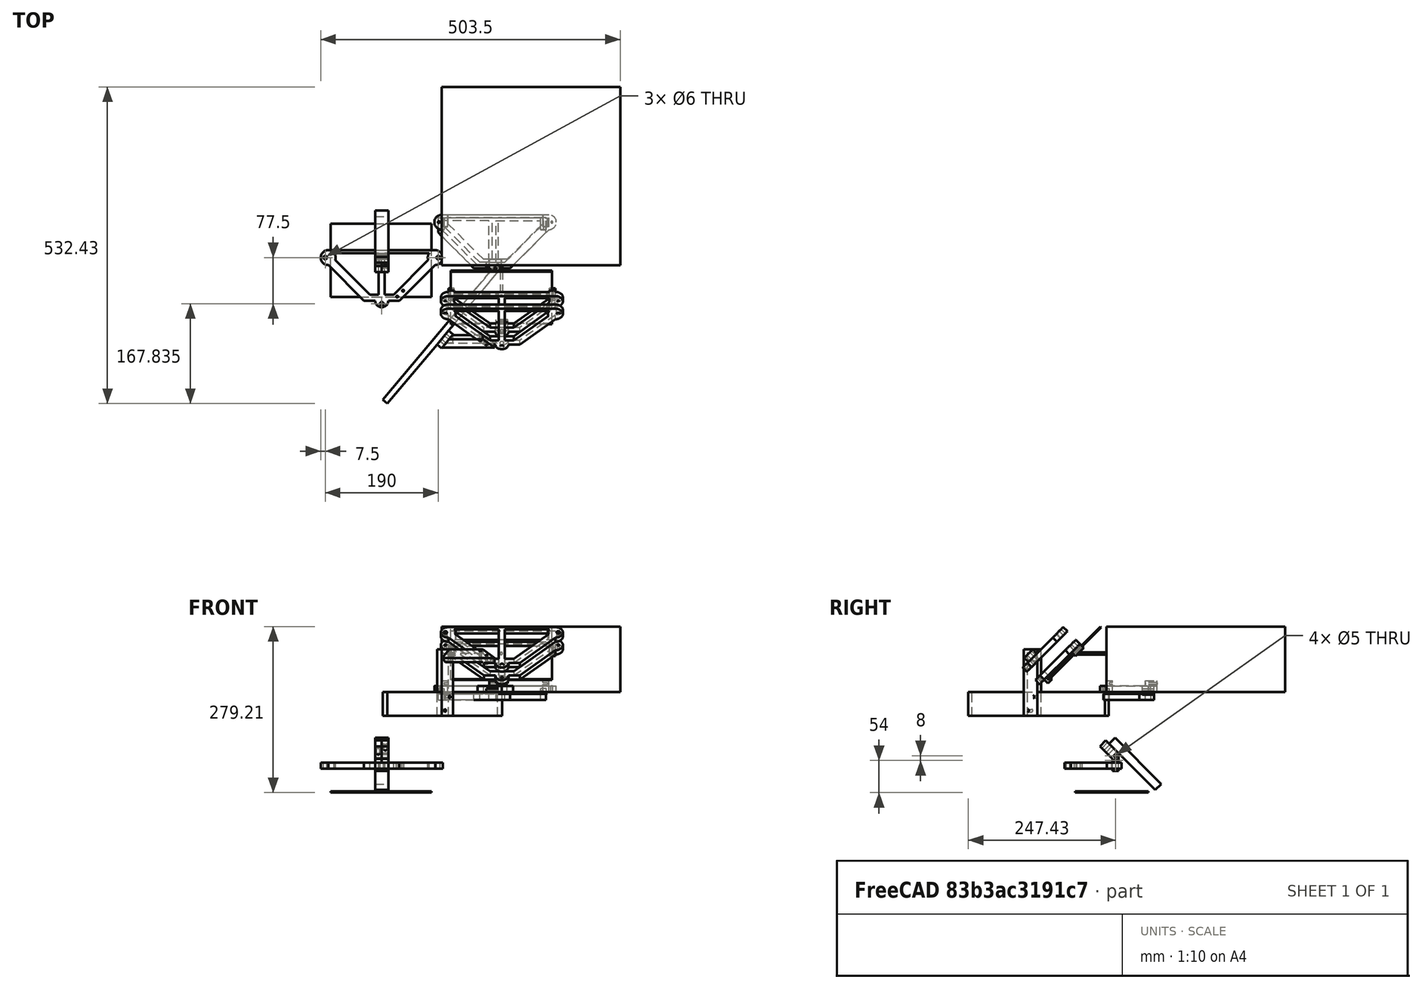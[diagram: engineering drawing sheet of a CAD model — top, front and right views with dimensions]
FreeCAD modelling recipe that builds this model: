
FCSTD DOCUMENT  (FreeCAD 0.19R24276 (Git))
Label: mirror-mount
License: All rights reserved
LicenseURL: http://en.wikipedia.org/wiki/All_rights_reserved
objects: Part::Box×51, Part::Cylinder×41, Part::MultiFuse×32, Part::Cut×29, Part::Chamfer×13, Part::Mirroring×2, App::DocumentObjectGroup×1, Part::MultiCommon×1
note: 169 computed .brp shape members not serialized (recipe doc carries the construction recipe); baked Part::Feature solids carry a one-line shape summary decoded from their .brp

FEATURE [Part::Box] Box  label="Mirror"
  AttacherType = Attacher::AttachEngine3D
  Height = 2
  Length = 170
  Placement = pos=(185,-99,22) rot=(0,0.924261,0.38176;3.14159rad)
  Width = 125
FEATURE [Part::Box] Box001  label="Cube001"
  AttacherType = Attacher::AttachEngine3D
  Height = 10
  Length = 10
  Placement = pos=(-5,0,-4) rot=(0,0,1;0rad)
  Width = 20
FEATURE [Part::Box] Box002  label="Cube002"
  AttacherType = Attacher::AttachEngine3D
  Height = 3
  Length = 10
  Placement = pos=(0,-3,-1) rot=(0,0,1;0rad)
  Width = 26
FEATURE [Part::Cut] Cut
  Base = -> Box001
  Placement = pos=(-1,60,0) rot=(0,0,1;0rad)
  Tool = -> Box002
FEATURE [Part::Box] Box003  label="Cube003"
  AttacherType = Attacher::AttachEngine3D
  Height = 10
  Length = 10
  Placement = pos=(-5,0,-4) rot=(0,0,1;0rad)
  Width = 20
FEATURE [Part::Box] Box004  label="Cube004"
  AttacherType = Attacher::AttachEngine3D
  Height = 3
  Length = 10
  Placement = pos=(0,-3,-1) rot=(0,0,1;0rad)
  Width = 26
FEATURE [Part::Cut] Cut001
  Base = -> Box003
  Placement = pos=(0,60,0) rot=(0,0,1;0rad)
  Tool = -> Box004
FEATURE [Part::Box] Box005  label="Cube005"
  AttacherType = Attacher::AttachEngine3D
  Height = 10
  Length = 10
  Placement = pos=(-5,0,-4) rot=(0,0,1;0rad)
  Width = 20
FEATURE [Part::Box] Box006  label="Cube006"
  AttacherType = Attacher::AttachEngine3D
  Height = 3
  Length = 10
  Placement = pos=(0,-3,-1) rot=(0,0,1;0rad)
  Width = 26
FEATURE [Part::Cut] Cut002
  Base = -> Box005
  Placement = pos=(95,0,0) rot=(0,0,1;1.5708rad)
  Tool = -> Box006
FEATURE [Part::Mirroring] Part__Mirroring  label="Cut001 (Mirror #1)"
  Base = (0,0,0)
  Normal = (1,0,0)
  Placement = pos=(171,0,0) rot=(0,0,1;0rad)
  Source = -> Cut001
FEATURE [Part::Box] Box007  label="Cube007"
  AttacherType = Attacher::AttachEngine3D
  Height = 10
  Length = 181
  Placement = pos=(-6,-5,-13) rot=(0,0,1;0rad)
  Width = 85
FEATURE [Part::Chamfer] Chamfer
  Base = -> Box007
  Edges = 1 edges r=60: [Edge1]
FEATURE [Part::Chamfer] Chamfer001
  Base = -> Chamfer
  Edges = 1 edges r=60: [Edge15]
FEATURE [Part::Box] Box008  label="Cube008"
  AttacherType = Attacher::AttachEngine3D
  Height = 25
  Length = 75
  Placement = pos=(4,5,-19) rot=(0,0,1;0rad)
  Width = 70
FEATURE [Part::Chamfer] Chamfer002
  Base = -> Box008
  Edges = 1 edges r=60: [Edge1]
FEATURE [Part::Box] Box009  label="Cube009"
  AttacherType = Attacher::AttachEngine3D
  Height = 25
  Length = 75
  Placement = pos=(4,5,-19) rot=(0,0,1;0rad)
  Width = 70
FEATURE [Part::Chamfer] Chamfer003
  Base = -> Box009
  Edges = 1 edges r=60: [Edge1]
FEATURE [Part::Mirroring] Part__Mirroring001  label="Chamfer003 (Mirror #2)"
  Base = (0,0,0)
  Normal = (1,0,0)
  Placement = pos=(170,0,0) rot=(0,0,1;0rad)
  Source = -> Chamfer003
FEATURE [Part::MultiFuse] Fusion
  Shapes = -> [Chamfer002,Part__Mirroring001]
FEATURE [Part::MultiFuse] Fusion001
  Shapes = -> [Chamfer001,Cut,Cut002,Part__Mirroring]
FEATURE [Part::Cut] Cut003
  Base = -> Fusion001
  Tool = -> Fusion
FEATURE [Part::Box] Box010  label="Projector"
  AttacherType = Attacher::AttachEngine3D
  Height = 110
  Length = 300
  Width = 300
FEATURE [Part::Cylinder] Cylinder  label="Lens Centre"
  Angle = 360
  AttacherType = Attacher::AttachEngine3D
  Height = 50
  Placement = pos=(100,0,65) rot=(1,0,0;1.5708rad)
  Radius = 2
FEATURE [Part::Box] Box011  label="Wooden Support"
  AttacherType = Attacher::AttachEngine3D
  Height = 40
  Length = 10
  Placement = pos=(-99,-226,-40) rot=(0,0,-1;0.698132rad)
  Width = 300
FEATURE [Part::Box] Box012  label="Cube012"
  AttacherType = Attacher::AttachEngine3D
  Height = 10
  Length = 180
  Width = 85
FEATURE [Part::Box] Box013  label="Cube013"
  AttacherType = Attacher::AttachEngine3D
  Height = 10
  Length = 10
  Placement = pos=(0,65,9) rot=(0,0,1;0rad)
  Width = 20
FEATURE [Part::Box] Box014  label="Cube014"
  AttacherType = Attacher::AttachEngine3D
  Height = 10
  Length = 20
  Placement = pos=(80,0,9) rot=(0,0,1;0rad)
  Width = 10
FEATURE [Part::Box] Box015  label="Cube015"
  AttacherType = Attacher::AttachEngine3D
  Height = 10
  Length = 10
  Placement = pos=(170,65,9) rot=(0,0,1;0rad)
  Width = 20
FEATURE [Part::Box] Box016  label="Cube016"
  AttacherType = Attacher::AttachEngine3D
  Height = 3
  Length = 26
  Placement = pos=(76.5,5,13) rot=(0,0,1;0rad)
  Width = 10
FEATURE [Part::Cut] Cut004
  Base = -> Box014
  Tool = -> Box016
FEATURE [Part::Box] Box017  label="Cube017"
  AttacherType = Attacher::AttachEngine3D
  Height = 3
  Length = 10
  Placement = pos=(167.5,62,13) rot=(0,0,1;0rad)
  Width = 26
FEATURE [Part::Box] Box018  label="Cube018"
  AttacherType = Attacher::AttachEngine3D
  Height = 3
  Length = 10
  Placement = pos=(3.5,62,13) rot=(0,0,1;0rad)
  Width = 26
FEATURE [Part::Cut] Cut005
  Base = -> Box013
  Tool = -> Box018
FEATURE [Part::Cut] Cut006
  Base = -> Box015
  Tool = -> Box017
FEATURE [Part::Chamfer] Chamfer004
  Base = -> Box012
  Edges = 2 edges r=60: [Edge1,Edge5]
FEATURE [Part::Box] Box019  label="Cube019"
  AttacherType = Attacher::AttachEngine3D
  Height = 25
  Length = 75
  Placement = pos=(10,10,-6) rot=(0,0,1;0rad)
  Width = 70
FEATURE [Part::Box] Box020  label="Cube020"
  AttacherType = Attacher::AttachEngine3D
  Height = 25
  Length = 75
  Placement = pos=(95,10,-6) rot=(0,0,1;0rad)
  Width = 70
FEATURE [Part::MultiFuse] Fusion002  label="Square Holes"
  Shapes = -> [Box019,Box020]
FEATURE [Part::Chamfer] Chamfer005  label="Chamfer Square Holes"
  Base = -> Fusion002
  Edges = 2 edges r=60: [Edge1,Edge17]
FEATURE [Part::MultiFuse] Fusion003  label="Square Clips"
  Shapes = -> [Cut006,Cut005,Cut004]
FEATURE [App::DocumentObjectGroup] Group  label="Old"
  Group = -> [Cut003]
FEATURE [Part::Box] Box021  label="Cube021"
  AttacherType = Attacher::AttachEngine3D
  Height = 10
  Length = 180
  Placement = pos=(0,0,-30) rot=(0,0,1;0rad)
  Width = 85
FEATURE [Part::Box] Box022  label="Cube022"
  AttacherType = Attacher::AttachEngine3D
  Height = 25
  Length = 75
  Placement = pos=(10,10,-37) rot=(0,0,1;0rad)
  Width = 70
FEATURE [Part::Chamfer] Chamfer006
  Base = -> Box021
  Edges = 2 edges r=60: [Edge1,Edge5]
FEATURE [Part::Box] Box023  label="Cube023"
  AttacherType = Attacher::AttachEngine3D
  Height = 25
  Length = 75
  Placement = pos=(95,10,-37) rot=(0,0,1;0rad)
  Width = 70
FEATURE [Part::MultiFuse] Fusion005
  Shapes = -> [Box022,Box023]
FEATURE [Part::Chamfer] Chamfer007
  Base = -> Fusion005
  Edges = 2 edges r=60: [Edge1,Edge17]
FEATURE [Part::Cut] Cut008
  Base = -> Chamfer006
  Tool = -> Chamfer007
FEATURE [Part::Cylinder] Cylinder001  label="Cylinder"
  Angle = 360
  AttacherType = Attacher::AttachEngine3D
  Height = 17
  Placement = pos=(90,-5,-6) rot=(0,0,1;0rad)
  Radius = 1.6
FEATURE [Part::Cylinder] Cylinder002
  Angle = 360
  AttacherType = Attacher::AttachEngine3D
  Height = 10
  Placement = pos=(90,0,0) rot=(0,0,1;0rad)
  Radius = 11
FEATURE [Part::Cylinder] Cylinder003
  Angle = 360
  AttacherType = Attacher::AttachEngine3D
  Height = 10
  Placement = pos=(180,72.5,0) rot=(0,0,1;0rad)
  Radius = 12.5
FEATURE [Part::Cylinder] Cylinder004
  Angle = 360
  AttacherType = Attacher::AttachEngine3D
  Height = 10
  Placement = pos=(0,72.5,0) rot=(0,0,1;0rad)
  Radius = 12.5
FEATURE [Part::MultiFuse] Fusion006  label="Bumps"
  Shapes = -> [Cylinder002,Cylinder003,Cylinder004]
FEATURE [Part::MultiFuse] Fusion007
  Shapes = -> [Fusion006,Chamfer004]
FEATURE [Part::Cut] Cut009
  Base = -> Fusion007
  Tool = -> Chamfer005
FEATURE [Part::Cylinder] Cylinder005
  Angle = 360
  AttacherType = Attacher::AttachEngine3D
  Height = 17
  Placement = pos=(185,72.5,-2) rot=(0,0,1;0rad)
  Radius = 1.6
FEATURE [Part::Cylinder] Cylinder006
  Angle = 360
  AttacherType = Attacher::AttachEngine3D
  Height = 17
  Placement = pos=(-5,72.5,-3) rot=(0,0,1;0rad)
  Radius = 1.6
FEATURE [Part::MultiFuse] Fusion008  label="M3 ST Holes"
  Shapes = -> [Cylinder005,Cylinder001,Cylinder006]
FEATURE [Part::Cut] Cut010
  Base = -> Cut009
  Tool = -> Fusion008
FEATURE [Part::MultiFuse] Fusion009  label="Mount - laying flat"
  Shapes = -> [Cut010,Fusion003]
FEATURE [Part::Cylinder] Cylinder007
  Angle = 360
  AttacherType = Attacher::AttachEngine3D
  Height = 10
  Placement = pos=(90,0,-30) rot=(0,0,1;0rad)
  Radius = 11
FEATURE [Part::Cylinder] Cylinder008
  Angle = 360
  AttacherType = Attacher::AttachEngine3D
  Height = 10
  Placement = pos=(180,72.5,-30) rot=(0,0,1;0rad)
  Radius = 12.5
FEATURE [Part::Cylinder] Cylinder009
  Angle = 360
  AttacherType = Attacher::AttachEngine3D
  Height = 10
  Placement = pos=(0,72.5,-30) rot=(0,0,1;0rad)
  Radius = 12.5
FEATURE [Part::Cylinder] Cylinder010
  Angle = 360
  AttacherType = Attacher::AttachEngine3D
  Height = 17
  Placement = pos=(185,72.5,-33) rot=(0,0,1;0rad)
  Radius = 3
FEATURE [Part::Cylinder] Cylinder011
  Angle = 360
  AttacherType = Attacher::AttachEngine3D
  Height = 17
  Placement = pos=(90,-5,-33) rot=(0,0,1;0rad)
  Radius = 3
FEATURE [Part::Cylinder] Cylinder012
  Angle = 360
  AttacherType = Attacher::AttachEngine3D
  Height = 17
  Placement = pos=(-5,72.5,-33) rot=(0,0,1;0rad)
  Radius = 3
FEATURE [Part::MultiFuse] Fusion010  label="Bumps001"
  Shapes = -> [Cylinder007,Cylinder008,Cylinder009]
FEATURE [Part::MultiFuse] Fusion011  label="Large Holes"
  Shapes = -> [Cylinder010,Cylinder011,Cylinder012]
FEATURE [Part::MultiFuse] Fusion012
  Shapes = -> [Cut008,Fusion010]
FEATURE [Part::Cut] Cut011
  Base = -> Fusion012
  Placement = pos=(191,-112,28) rot=(0,0.924261,0.38176;3.14159rad)
  Tool = -> Fusion011
FEATURE [Part::Box] Box024  label="Cube024"
  AttacherType = Attacher::AttachEngine3D
  Height = 10
  Length = 180
  Width = 85
FEATURE [Part::Box] Box025  label="Cube025"
  AttacherType = Attacher::AttachEngine3D
  Height = 10
  Length = 10
  Placement = pos=(0,65,9) rot=(0,0,1;0rad)
  Width = 20
FEATURE [Part::Box] Box026  label="Cube026"
  AttacherType = Attacher::AttachEngine3D
  Height = 10
  Length = 20
  Placement = pos=(80,0,9) rot=(0,0,1;0rad)
  Width = 10
FEATURE [Part::Box] Box027  label="Cube027"
  AttacherType = Attacher::AttachEngine3D
  Height = 10
  Length = 10
  Placement = pos=(170,65,9) rot=(0,0,1;0rad)
  Width = 20
FEATURE [Part::Box] Box028  label="Cube028"
  AttacherType = Attacher::AttachEngine3D
  Height = 3
  Length = 26
  Placement = pos=(76.5,5,13) rot=(0,0,1;0rad)
  Width = 10
FEATURE [Part::Cut] Cut012
  Base = -> Box026
  Tool = -> Box028
FEATURE [Part::Box] Box029  label="Cube029"
  AttacherType = Attacher::AttachEngine3D
  Height = 3
  Length = 10
  Placement = pos=(167.5,62,13) rot=(0,0,1;0rad)
  Width = 26
FEATURE [Part::Box] Box030  label="Cube030"
  AttacherType = Attacher::AttachEngine3D
  Height = 3
  Length = 10
  Placement = pos=(3.5,62,13) rot=(0,0,1;0rad)
  Width = 26
FEATURE [Part::Cut] Cut013
  Base = -> Box025
  Tool = -> Box030
FEATURE [Part::Cut] Cut014
  Base = -> Box027
  Tool = -> Box029
FEATURE [Part::Chamfer] Chamfer008
  Base = -> Box024
  Edges = 2 edges r=60: [Edge1,Edge5]
FEATURE [Part::Box] Box031  label="Cube031"
  AttacherType = Attacher::AttachEngine3D
  Height = 25
  Length = 75
  Placement = pos=(10,10,-6) rot=(0,0,1;0rad)
  Width = 70
FEATURE [Part::Box] Box032  label="Cube032"
  AttacherType = Attacher::AttachEngine3D
  Height = 25
  Length = 75
  Placement = pos=(95,10,-6) rot=(0,0,1;0rad)
  Width = 70
FEATURE [Part::MultiFuse] Fusion013  label="Square Holes001"
  Shapes = -> [Box031,Box032]
FEATURE [Part::Chamfer] Chamfer009  label="Chamfer Square Holes001"
  Base = -> Fusion013
  Edges = 2 edges r=60: [Edge1,Edge17]
FEATURE [Part::MultiFuse] Fusion014  label="Square Clips001"
  Shapes = -> [Cut014,Cut013,Cut012]
FEATURE [Part::Cylinder] Cylinder013
  Angle = 360
  AttacherType = Attacher::AttachEngine3D
  Height = 17
  Placement = pos=(90,-5,-6) rot=(0,0,1;0rad)
  Radius = 1.6
FEATURE [Part::Cylinder] Cylinder014
  Angle = 360
  AttacherType = Attacher::AttachEngine3D
  Height = 10
  Placement = pos=(90,0,0) rot=(0,0,1;0rad)
  Radius = 11
FEATURE [Part::Cylinder] Cylinder015
  Angle = 360
  AttacherType = Attacher::AttachEngine3D
  Height = 10
  Placement = pos=(180,72.5,0) rot=(0,0,1;0rad)
  Radius = 12.5
FEATURE [Part::Cylinder] Cylinder016
  Angle = 360
  AttacherType = Attacher::AttachEngine3D
  Height = 10
  Placement = pos=(0,72.5,0) rot=(0,0,1;0rad)
  Radius = 12.5
FEATURE [Part::MultiFuse] Fusion015  label="Bumps002"
  Shapes = -> [Cylinder014,Cylinder015,Cylinder016]
FEATURE [Part::MultiFuse] Fusion016
  Shapes = -> [Fusion015,Chamfer008]
FEATURE [Part::Cut] Cut015
  Base = -> Fusion016
  Tool = -> Chamfer009
FEATURE [Part::Cylinder] Cylinder017
  Angle = 360
  AttacherType = Attacher::AttachEngine3D
  Height = 17
  Placement = pos=(185,72.5,-2) rot=(0,0,1;0rad)
  Radius = 1.6
FEATURE [Part::Cylinder] Cylinder018
  Angle = 360
  AttacherType = Attacher::AttachEngine3D
  Height = 17
  Placement = pos=(-5,72.5,-3) rot=(0,0,1;0rad)
  Radius = 1.6
FEATURE [Part::MultiFuse] Fusion017  label="M3 ST Holes001"
  Shapes = -> [Cylinder017,Cylinder013,Cylinder018]
FEATURE [Part::Cut] Cut016
  Base = -> Cut015
  Tool = -> Fusion017
FEATURE [Part::MultiFuse] Fusion018  label="Mount001"
  Placement = pos=(191,-112,28) rot=(0,0.924261,0.38176;3.14159rad)
  Shapes = -> [Cut016,Fusion014]
FEATURE [Part::Box] Box033  label="Wooden Support001"
  AttacherType = Attacher::AttachEngine3D
  Height = 112
  Length = 10
  Placement = pos=(-8,-133,-40) rot=(0,0,-1;0.698132rad)
  Width = 30
FEATURE [Part::Box] Box034  label="Cube"
  AttacherType = Attacher::AttachEngine3D
  Height = 10
  Length = 90
  Placement = pos=(89,-138.47,57.61) rot=(0,0.924261,0.38176;3.14159rad)
  Width = 20
FEATURE [Part::Box] Box035  label="Wooden Support002"
  AttacherType = Attacher::AttachEngine3D
  Height = 135
  Length = 10
  Placement = pos=(-20,-133,-40) rot=(0,0,-1;0.698132rad)
  Width = 30
FEATURE [Part::Cut] Cut017
  Base = -> Box034
  Tool = -> Box035
FEATURE [Part::Chamfer] Chamfer010
  Base = -> Cut017
  Edges = 1 edges r=19.99: [Edge3]
FEATURE [Part::Cylinder] Cylinder019
  Angle = 360
  AttacherType = Attacher::AttachEngine3D
  Height = 50
  Placement = pos=(75,-154,80) rot=(0,0.924261,0.38176;3.14159rad)
  Radius = 1.8
FEATURE [Part::Cylinder] Cylinder020
  Angle = 360
  AttacherType = Attacher::AttachEngine3D
  Height = 50
  Placement = pos=(65,-140,80) rot=(0,0.924261,0.38176;3.14159rad)
  Radius = 1.8
FEATURE [Part::Cylinder] Cylinder021
  Angle = 360
  AttacherType = Attacher::AttachEngine3D
  Height = 50
  Placement = pos=(75,-154,80) rot=(0,0.924261,0.38176;3.14159rad)
  Radius = 1.6
FEATURE [Part::Cylinder] Cylinder022
  Angle = 360
  AttacherType = Attacher::AttachEngine3D
  Height = 50
  Placement = pos=(65,-140,80) rot=(0,0.924261,0.38176;3.14159rad)
  Radius = 1.6
FEATURE [Part::MultiFuse] Fusion019  label="Clearance Holes"
  Shapes = -> [Cylinder019,Cylinder020]
FEATURE [Part::Cut] Cut018
  Base = -> Chamfer010
  Tool = -> Fusion019
FEATURE [Part::MultiFuse] Fusion020  label="M3 ST Holes002"
  Shapes = -> [Cylinder021,Cylinder022]
FEATURE [Part::Cut] Cut019  label="Mount Carrier"
  Base = -> Cut011
  Tool = -> Fusion020
FEATURE [Part::MultiFuse] Fusion021
  Shapes = -> [Cut018,Box033]
FEATURE [Part::Cylinder] Cylinder023
  Angle = 360
  AttacherType = Attacher::AttachEngine3D
  Height = 52
  Placement = pos=(25.77,-134.121,-8) rot=(0.68362,-0.255595,-0.68362;3.64207rad)
  Radius = 2.2
FEATURE [Part::Cylinder] Cylinder024
  Angle = 360
  AttacherType = Attacher::AttachEngine3D
  Height = 52
  Placement = pos=(7.77,-134.121,-31) rot=(0.68362,-0.255595,-0.68362;3.64207rad)
  Radius = 2.2
FEATURE [Part::MultiFuse] Fusion022  label="M4 Holes"
  Shapes = -> [Cylinder024,Cylinder023]
FEATURE [Part::Cut] Cut020
  Base = -> Fusion021
  Tool = -> Fusion022
FEATURE [Part::Box] Box036  label="Cube033"
  AttacherType = Attacher::AttachEngine3D
  Height = 13
  Length = 13
  Placement = pos=(5,-131,52) rot=(0,0,1;0rad)
  Width = 15
FEATURE [Part::Box] Box037  label="Wooden Support003"
  AttacherType = Attacher::AttachEngine3D
  Height = 135
  Length = 10
  Placement = pos=(-20,-133,-40) rot=(0,0,-1;0.698132rad)
  Width = 30
FEATURE [Part::Cut] Cut021
  Base = -> Box036
  Tool = -> Box037
FEATURE [Part::MultiFuse] Fusion023  label="Bracket"
  Shapes = -> [Cut020,Cut021]
FEATURE [Part::Box] Box038  label="Cube034"
  AttacherType = Attacher::AttachEngine3D
  Height = 10
  Length = 180
  Placement = pos=(0,0,-30) rot=(0,0,1;0rad)
  Width = 85
FEATURE [Part::Box] Box039  label="Cube035"
  AttacherType = Attacher::AttachEngine3D
  Height = 25
  Length = 75
  Placement = pos=(10,10,-37) rot=(0,0,1;0rad)
  Width = 70
FEATURE [Part::Chamfer] Chamfer011
  Base = -> Box038
  Edges = 2 edges r=60: [Edge1,Edge5]
FEATURE [Part::Box] Box040  label="Cube036"
  AttacherType = Attacher::AttachEngine3D
  Height = 25
  Length = 75
  Placement = pos=(95,10,-37) rot=(0,0,1;0rad)
  Width = 70
FEATURE [Part::MultiFuse] Fusion024
  Shapes = -> [Box039,Box040]
FEATURE [Part::Chamfer] Chamfer012
  Base = -> Fusion024
  Edges = 2 edges r=60: [Edge1,Edge17]
FEATURE [Part::Cut] Cut022
  Base = -> Chamfer011
  Tool = -> Chamfer012
FEATURE [Part::Cylinder] Cylinder025
  Angle = 360
  AttacherType = Attacher::AttachEngine3D
  Height = 10
  Placement = pos=(90,0,-30) rot=(0,0,1;0rad)
  Radius = 11
FEATURE [Part::Cylinder] Cylinder026
  Angle = 360
  AttacherType = Attacher::AttachEngine3D
  Height = 10
  Placement = pos=(180,72.5,-30) rot=(0,0,1;0rad)
  Radius = 12.5
FEATURE [Part::Cylinder] Cylinder027
  Angle = 360
  AttacherType = Attacher::AttachEngine3D
  Height = 10
  Placement = pos=(0,72.5,-30) rot=(0,0,1;0rad)
  Radius = 12.5
FEATURE [Part::Cylinder] Cylinder028
  Angle = 360
  AttacherType = Attacher::AttachEngine3D
  Height = 17
  Placement = pos=(185,72.5,-33) rot=(0,0,1;0rad)
  Radius = 3
FEATURE [Part::Cylinder] Cylinder029
  Angle = 360
  AttacherType = Attacher::AttachEngine3D
  Height = 17
  Placement = pos=(90,-5,-33) rot=(0,0,1;0rad)
  Radius = 3
FEATURE [Part::Cylinder] Cylinder030
  Angle = 360
  AttacherType = Attacher::AttachEngine3D
  Height = 17
  Placement = pos=(-5,72.5,-33) rot=(0,0,1;0rad)
  Radius = 3
FEATURE [Part::MultiFuse] Fusion025  label="Bumps003"
  Shapes = -> [Cylinder025,Cylinder026,Cylinder027]
FEATURE [Part::MultiFuse] Fusion026  label="Large Holes001"
  Shapes = -> [Cylinder028,Cylinder029,Cylinder030]
FEATURE [Part::MultiFuse] Fusion027
  Shapes = -> [Cut022,Fusion025]
FEATURE [Part::Cut] Cut023
  Base = -> Fusion027
  Placement = pos=(191,-112,28) rot=(0,0.924261,0.38176;3.14159rad)
  Tool = -> Fusion026
FEATURE [Part::Cylinder] Cylinder031
  Angle = 360
  AttacherType = Attacher::AttachEngine3D
  Height = 50
  Placement = pos=(65,-140,80) rot=(0,0.924261,0.38176;3.14159rad)
  Radius = 1.6
FEATURE [Part::Cylinder] Cylinder032
  Angle = 360
  AttacherType = Attacher::AttachEngine3D
  Height = 50
  Placement = pos=(75,-154,80) rot=(0,0.924261,0.38176;3.14159rad)
  Radius = 1.6
FEATURE [Part::MultiFuse] Fusion028  label="M3 ST Holes003"
  Shapes = -> [Cylinder032,Cylinder031]
FEATURE [Part::Cut] Cut024  label="Mount Carrier001 laying flat"
  Base = -> Cut023
  Placement = pos=(0,0,0) rot=(0,0.924261,0.38176;3.14159rad)
  Tool = -> Fusion028
FEATURE [Part::Box] Box041  label="Mirror Flat"
  AttacherType = Attacher::AttachEngine3D
  Height = 2
  Length = 170
  Placement = pos=(-187,-53,-169) rot=(0,0,1;0rad)
  Width = 123
FEATURE [Part::Box] Box042  label="Cube038"
  AttacherType = Attacher::AttachEngine3D
  Height = 11
  Length = 11
  Placement = pos=(-106.5,10,-129.5) rot=(0,0,1;0rad)
  Width = 10
FEATURE [Part::Box] Box043  label="Cube039"
  AttacherType = Attacher::AttachEngine3D
  Height = 30
  Length = 22
  Placement = pos=(-112,10,-132.5) rot=(0,0,1;0rad)
  Width = 10
FEATURE [Part::Box] Box044  label="Cube040"
  AttacherType = Attacher::AttachEngine3D
  Height = 30
  Length = 22
  Placement = pos=(-112,10,-112.5) rot=(1,0,0;0.785398rad)
  Width = 14.1
FEATURE [Part::Box] Box045  label="45 degree piece"
  AttacherType = Attacher::AttachEngine3D
  Height = 110
  Length = 22
  Placement = pos=(-112,82,-164.5) rot=(1,0,0;0.785398rad)
  Width = 14.1
FEATURE [Part::Cylinder] Cylinder033
  Angle = 360
  AttacherType = Attacher::AttachEngine3D
  Height = 24
  Placement = pos=(-95,-8.48528,-98.4853) rot=(1,0,0;5.49779rad)
  Radius = 2.5
FEATURE [Part::Cylinder] Cylinder034
  Angle = 360
  AttacherType = Attacher::AttachEngine3D
  Height = 24
  Placement = pos=(-107,-2.49,-106.49) rot=(-1,0,0;0.785398rad)
  Radius = 2.5
FEATURE [Part::Cylinder] Cylinder035
  Angle = 360
  AttacherType = Attacher::AttachEngine3D
  Height = 32
  Placement = pos=(-118,15,-107) rot=(0,1,0;1.5708rad)
  Radius = 2.5
FEATURE [Part::Cylinder] Cylinder036
  Angle = 360
  AttacherType = Attacher::AttachEngine3D
  Height = 32
  Placement = pos=(-118,15,-115) rot=(0,1,0;1.5708rad)
  Radius = 2.5
FEATURE [Part::Box] Box046  label="Cube041"
  AttacherType = Attacher::AttachEngine3D
  Height = 59
  Length = 22
  Placement = pos=(-123,-16,-135.5) rot=(0,0,1;0rad)
  Width = 44
FEATURE [Part::MultiFuse] Fusion029
  Shapes = -> [Box043,Box044]
FEATURE [Part::Cut] Cut025
  Base = -> Fusion029
  Tool = -> Box042
FEATURE [Part::MultiFuse] Fusion030
  Shapes = -> [Cylinder036,Cylinder033,Cylinder034,Cylinder035]
FEATURE [Part::Cut] Cut026
  Base = -> Cut025
  Tool = -> Fusion030
FEATURE [Part::Box] Box047  label="Cube042"
  AttacherType = Attacher::AttachEngine3D
  Height = 11
  Length = 11
  Placement = pos=(-106.5,10,-129.5) rot=(0,0,1;0rad)
  Width = 10
FEATURE [Part::Box] Box048  label="Cube043"
  AttacherType = Attacher::AttachEngine3D
  Height = 30
  Length = 22
  Placement = pos=(-112,10,-112.5) rot=(1,0,0;0.785398rad)
  Width = 14.1
FEATURE [Part::Box] Box049  label="Cube044"
  AttacherType = Attacher::AttachEngine3D
  Height = 30
  Length = 22
  Placement = pos=(-112,10,-132.5) rot=(0,0,1;0rad)
  Width = 10
FEATURE [Part::Cylinder] Cylinder037
  Angle = 360
  AttacherType = Attacher::AttachEngine3D
  Height = 24
  Placement = pos=(-95,-8.48528,-98.4853) rot=(-1,0,0;0.785398rad)
  Radius = 2.5
FEATURE [Part::Cylinder] Cylinder038
  Angle = 360
  AttacherType = Attacher::AttachEngine3D
  Height = 24
  Placement = pos=(-107,-2.49,-106.49) rot=(-1,0,0;0.785398rad)
  Radius = 2.5
FEATURE [Part::Cylinder] Cylinder039
  Angle = 360
  AttacherType = Attacher::AttachEngine3D
  Height = 32
  Placement = pos=(-118,15,-107) rot=(0,1,0;1.5708rad)
  Radius = 2.5
FEATURE [Part::MultiFuse] Fusion032
  Shapes = -> [Box049,Box048]
FEATURE [Part::Cylinder] Cylinder040
  Angle = 360
  AttacherType = Attacher::AttachEngine3D
  Height = 32
  Placement = pos=(-118,15,-115) rot=(0,1,0;1.5708rad)
  Radius = 2.5
FEATURE [Part::MultiFuse] Fusion031
  Shapes = -> [Cylinder040,Cylinder037,Cylinder038,Cylinder039]
FEATURE [Part::Cut] Cut028
  Base = -> Fusion032
  Tool = -> Box047
FEATURE [Part::Cut] Cut027
  Base = -> Cut028
  Tool = -> Fusion031
FEATURE [Part::Box] Box050  label="Cube045"
  AttacherType = Attacher::AttachEngine3D
  Height = 59
  Length = 22
  Placement = pos=(-123,-16,-135.5) rot=(0,0,1;0rad)
  Width = 44
FEATURE [Part::Cut] Cut029
  Base = -> Cut026
  Tool = -> Box046
FEATURE [Part::MultiCommon] Common
  Shapes = -> [Box050,Cut027]
